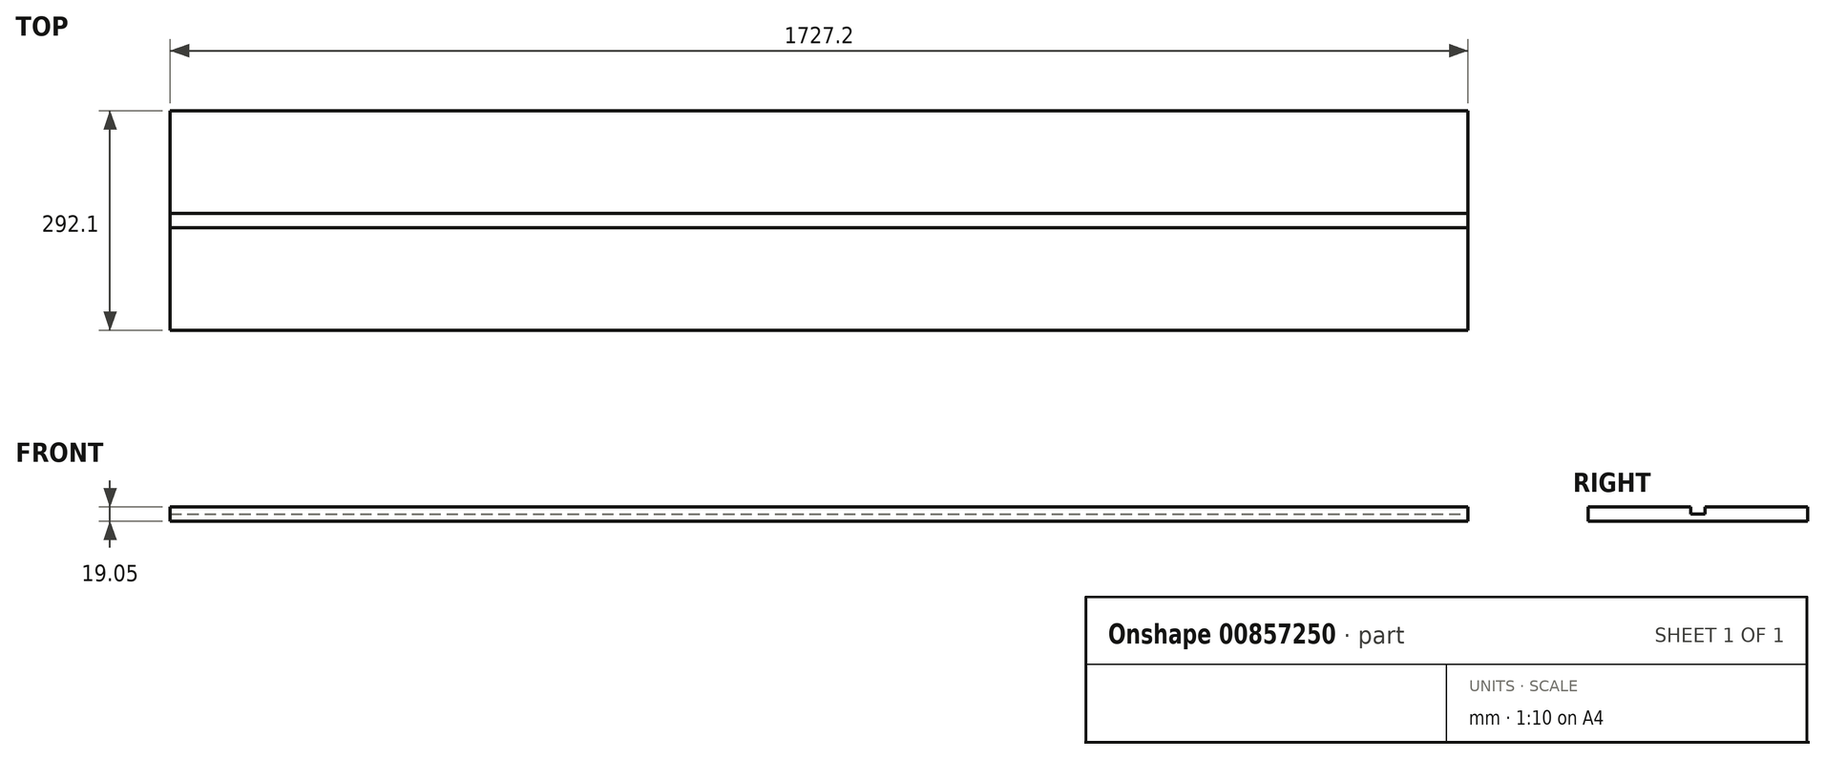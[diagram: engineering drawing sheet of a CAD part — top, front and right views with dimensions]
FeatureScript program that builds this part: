
annotation { "Feature Type Name" : "Feature", "Feature Type Description" : "" }
export const myFeature = defineFeature(function(context is Context, id is Id, definition is map)
    precondition{}
    {
        {
            var Q0;
            Q0=qCreatedBy(makeId("Top.planeOp"),FACE);
            var sketch = newSketch(context, id + "F0", { "sketchPlane" : qUnion([Q0])});
            skLineSegment(sketch, "E0.bottom", {"start": v(-2362.3, 257.66) * mm, "end": v(-635.1, 257.66) * mm});
            skLineSegment(sketch, "E0.top", {"start": v(-2362.3, -34.44) * mm, "end": v(-635.1, -34.44) * mm});
            skLineSegment(sketch, "E0.left", {"start": v(-2362.3, 257.66) * mm, "end": v(-2362.3, -34.44) * mm});
            skLineSegment(sketch, "E0.right", {"start": v(-635.1, 257.66) * mm, "end": v(-635.1, -34.44) * mm});
            skSolve(sketch);
        }
        {
            var Q0;
            Q0=makeQuery(id+"F0.imprint","IMPRINT",FACE,{"disambiguationData":[TD([[makeQuery(id+"F0.imprint","IMPRINT",EDGE,{"derivedFrom":sQuery(id+"F0.wireOp",EDGE,"E0.bottom")}),-1.0]])]});
            extrude(context, id + "F1", {"entities" : qUnion([Q0]), "depth" : 19.05 * mm, "offsetDistance" : 25.4 * mm});
        }
        {
            var Q0;
            Q0=makeQuery(id+"F1.opExtrude","SWEPT_FACE",FACE,{"disambiguationData":[OSD([sQuery(id+"F0.wireOp",EDGE,"E0.right")])]});
            var sketch = newSketch(context, id + "F2", { "sketchPlane" : qUnion([Q0])});
            skLineSegment(sketch, "E1.bottom", {"start": v(102.08, 9.52) * mm, "end": v(121.13, 9.52) * mm});
            skLineSegment(sketch, "E1.top", {"start": v(102.08, 28.57) * mm, "end": v(121.13, 28.57) * mm});
            skLineSegment(sketch, "E1.left", {"start": v(102.08, 9.52) * mm, "end": v(102.08, 28.57) * mm});
            skLineSegment(sketch, "E1.right", {"start": v(121.13, 9.52) * mm, "end": v(121.13, 28.57) * mm});
            skPoint(sketch, "E1.middle", {"position": v(111.6, 19.05) * mm});
            skSolve(sketch);
        }
        {
            var Q0;
            {var subQ0=sQuery(id+"F2.wireOp",EDGE,"E1.bottom");Q0=makeQuery(id+"F2.imprint","IMPRINT",FACE,{"disambiguationData":[TD([[makeQuery(id+"F2.imprint","IMPRINT",EDGE,{"derivedFrom":subQ0}),1.0]])]});}
            extrude(context, id + "F3", {"entities" : qUnion([Q0]), "operationType" : NewBodyOperationType.REMOVE, "oppositeDirection" : true, "depth" : 2438.4 * mm, "offsetDistance" : 25.4 * mm});
        }
    });
